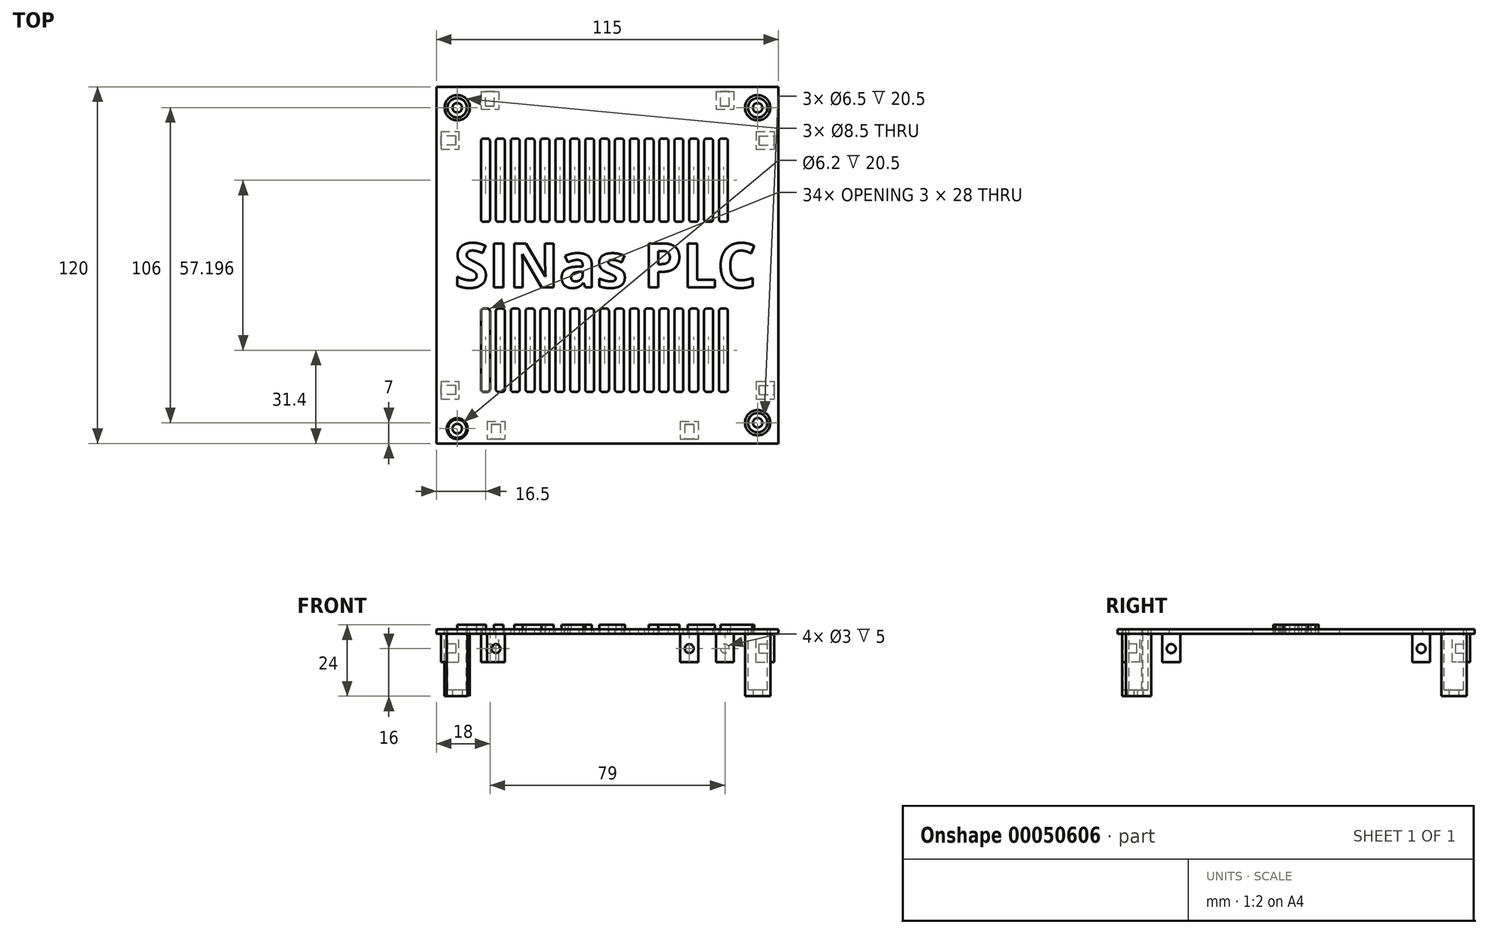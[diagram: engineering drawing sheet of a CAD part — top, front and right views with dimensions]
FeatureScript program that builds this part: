
annotation { "Feature Type Name" : "Feature", "Feature Type Description" : "" }
export const myFeature = defineFeature(function(context is Context, id is Id, definition is map)
    precondition{}
    {
        {
            var Q0;
            Q0=qCreatedBy(makeId("Top.planeOp"),FACE);
            var sketch = newSketch(context, id + "F0", { "sketchPlane" : qUnion([Q0])});
            skLineSegment(sketch, "E0.bottom", {"start": v(-52.5, 65) * mm, "end": v(62.5, 65) * mm});
            skLineSegment(sketch, "E0.top", {"start": v(-52.5, -55) * mm, "end": v(62.5, -55) * mm});
            skLineSegment(sketch, "E0.left", {"start": v(-52.5, 65) * mm, "end": v(-52.5, -55) * mm});
            skLineSegment(sketch, "E0.right", {"start": v(62.5, 65) * mm, "end": v(62.5, -55) * mm});
            skCircle(sketch, "E1", {"center": v(-45.5, 58) * mm, "radius": 4.25 * mm});
            skCircle(sketch, "E2", {"center": v(55.5, 58) * mm, "radius": 4.25 * mm});
            skCircle(sketch, "E3", {"center": v(55.5, -48) * mm, "radius": 4.25 * mm});
            skCircle(sketch, "E4", {"center": v(-45.5, -50) * mm, "radius": 3.5 * mm});
            skText(sketch, "E5", { "text": "SINas PLC", "fontName": "OpenSans-Bold.ttf"});
            skLineSegment(sketch, "E6.bottom", {"start": v(-36.7, 47.6) * mm, "end": v(-35.3, 47.6) * mm});
            skLineSegment(sketch, "E6.top", {"start": v(-36.7, 19.6) * mm, "end": v(-35.3, 19.6) * mm});
            skLineSegment(sketch, "E6.left", {"start": v(-37.5, 46.8) * mm, "end": v(-37.5, 20.4) * mm});
            skLineSegment(sketch, "E6.right", {"start": v(-34.5, 46.8) * mm, "end": v(-34.5, 20.4) * mm});
            skPoint(sketch, "E7.visualSharp", {"position": v(-37.5, 47.6) * mm});
            skArc(sketch, "E7.filletArc", {"start": v(-36.7, 47.6) * mm, "mid": v(-37.27, 47.36) * mm, "end": v(-37.5, 46.8) * mm});
            skPoint(sketch, "E8.visualSharp", {"position": v(-34.5, 47.6) * mm});
            skArc(sketch, "E8.filletArc", {"start": v(-34.5, 46.8) * mm, "mid": v(-34.73, 47.36) * mm, "end": v(-35.3, 47.6) * mm});
            skPoint(sketch, "E9.visualSharp", {"position": v(-37.5, 19.6) * mm});
            skArc(sketch, "E9.filletArc", {"start": v(-37.5, 20.4) * mm, "mid": v(-37.27, 19.83) * mm, "end": v(-36.7, 19.6) * mm});
            skPoint(sketch, "E10.visualSharp", {"position": v(-34.5, 19.6) * mm});
            skArc(sketch, "E10.filletArc", {"start": v(-35.3, 19.6) * mm, "mid": v(-34.73, 19.83) * mm, "end": v(-34.5, 20.4) * mm});
            skLineSegment(sketch, "E11.1.0.0", {"start": v(-29.5, 46.8) * mm, "end": v(-29.5, 20.4) * mm});
            skPoint(sketch, "E11.1.0.1", {"position": v(-32.5, 47.6) * mm});
            skPoint(sketch, "E11.1.0.2", {"position": v(-29.5, 47.6) * mm});
            skPoint(sketch, "E11.1.0.3", {"position": v(-32.5, 19.6) * mm});
            skLineSegment(sketch, "E11.1.0.4", {"start": v(-32.5, 46.8) * mm, "end": v(-32.5, 20.4) * mm});
            skPoint(sketch, "E11.1.0.5", {"position": v(-29.5, 19.6) * mm});
            skArc(sketch, "E11.1.0.6", {"start": v(-29.5, 46.8) * mm, "mid": v(-29.73, 47.36) * mm, "end": v(-30.3, 47.6) * mm});
            skLineSegment(sketch, "E11.1.0.7", {"start": v(-31.7, 19.6) * mm, "end": v(-30.3, 19.6) * mm});
            skLineSegment(sketch, "E11.1.0.8", {"start": v(-31.7, 47.6) * mm, "end": v(-30.3, 47.6) * mm});
            skArc(sketch, "E11.1.0.9", {"start": v(-31.7, 47.6) * mm, "mid": v(-32.27, 47.36) * mm, "end": v(-32.5, 46.8) * mm});
            skArc(sketch, "E11.1.0.10", {"start": v(-32.5, 20.4) * mm, "mid": v(-32.27, 19.83) * mm, "end": v(-31.7, 19.6) * mm});
            skArc(sketch, "E11.1.0.11", {"start": v(-30.3, 19.6) * mm, "mid": v(-29.73, 19.83) * mm, "end": v(-29.5, 20.4) * mm});
            skLineSegment(sketch, "E11.2.0.0", {"start": v(-24.5, 46.8) * mm, "end": v(-24.5, 20.4) * mm});
            skPoint(sketch, "E11.2.0.1", {"position": v(-27.5, 47.6) * mm});
            skPoint(sketch, "E11.2.0.2", {"position": v(-24.5, 47.6) * mm});
            skPoint(sketch, "E11.2.0.3", {"position": v(-27.5, 19.6) * mm});
            skLineSegment(sketch, "E11.2.0.4", {"start": v(-27.5, 46.8) * mm, "end": v(-27.5, 20.4) * mm});
            skPoint(sketch, "E11.2.0.5", {"position": v(-24.5, 19.6) * mm});
            skArc(sketch, "E11.2.0.6", {"start": v(-24.5, 46.8) * mm, "mid": v(-24.73, 47.36) * mm, "end": v(-25.3, 47.6) * mm});
            skLineSegment(sketch, "E11.2.0.7", {"start": v(-26.7, 19.6) * mm, "end": v(-25.3, 19.6) * mm});
            skLineSegment(sketch, "E11.2.0.8", {"start": v(-26.7, 47.6) * mm, "end": v(-25.3, 47.6) * mm});
            skArc(sketch, "E11.2.0.9", {"start": v(-26.7, 47.6) * mm, "mid": v(-27.27, 47.36) * mm, "end": v(-27.5, 46.8) * mm});
            skArc(sketch, "E11.2.0.10", {"start": v(-27.5, 20.4) * mm, "mid": v(-27.27, 19.83) * mm, "end": v(-26.7, 19.6) * mm});
            skArc(sketch, "E11.2.0.11", {"start": v(-25.3, 19.6) * mm, "mid": v(-24.73, 19.83) * mm, "end": v(-24.5, 20.4) * mm});
            skLineSegment(sketch, "E11.3.0.0", {"start": v(-19.5, 46.8) * mm, "end": v(-19.5, 20.4) * mm});
            skPoint(sketch, "E11.3.0.1", {"position": v(-22.5, 47.6) * mm});
            skPoint(sketch, "E11.3.0.2", {"position": v(-19.5, 47.6) * mm});
            skPoint(sketch, "E11.3.0.3", {"position": v(-22.5, 19.6) * mm});
            skLineSegment(sketch, "E11.3.0.4", {"start": v(-22.5, 46.8) * mm, "end": v(-22.5, 20.4) * mm});
            skPoint(sketch, "E11.3.0.5", {"position": v(-19.5, 19.6) * mm});
            skArc(sketch, "E11.3.0.6", {"start": v(-19.5, 46.8) * mm, "mid": v(-19.73, 47.36) * mm, "end": v(-20.3, 47.6) * mm});
            skLineSegment(sketch, "E11.3.0.7", {"start": v(-21.7, 19.6) * mm, "end": v(-20.3, 19.6) * mm});
            skLineSegment(sketch, "E11.3.0.8", {"start": v(-21.7, 47.6) * mm, "end": v(-20.3, 47.6) * mm});
            skArc(sketch, "E11.3.0.9", {"start": v(-21.7, 47.6) * mm, "mid": v(-22.27, 47.36) * mm, "end": v(-22.5, 46.8) * mm});
            skArc(sketch, "E11.3.0.10", {"start": v(-22.5, 20.4) * mm, "mid": v(-22.27, 19.83) * mm, "end": v(-21.7, 19.6) * mm});
            skArc(sketch, "E11.3.0.11", {"start": v(-20.3, 19.6) * mm, "mid": v(-19.73, 19.83) * mm, "end": v(-19.5, 20.4) * mm});
            skLineSegment(sketch, "E11.4.0.0", {"start": v(-14.5, 46.8) * mm, "end": v(-14.5, 20.4) * mm});
            skPoint(sketch, "E11.4.0.1", {"position": v(-17.5, 47.6) * mm});
            skPoint(sketch, "E11.4.0.2", {"position": v(-14.5, 47.6) * mm});
            skPoint(sketch, "E11.4.0.3", {"position": v(-17.5, 19.6) * mm});
            skLineSegment(sketch, "E11.4.0.4", {"start": v(-17.5, 46.8) * mm, "end": v(-17.5, 20.4) * mm});
            skPoint(sketch, "E11.4.0.5", {"position": v(-14.5, 19.6) * mm});
            skArc(sketch, "E11.4.0.6", {"start": v(-14.5, 46.8) * mm, "mid": v(-14.73, 47.36) * mm, "end": v(-15.3, 47.6) * mm});
            skLineSegment(sketch, "E11.4.0.7", {"start": v(-16.7, 19.6) * mm, "end": v(-15.3, 19.6) * mm});
            skLineSegment(sketch, "E11.4.0.8", {"start": v(-16.7, 47.6) * mm, "end": v(-15.3, 47.6) * mm});
            skArc(sketch, "E11.4.0.9", {"start": v(-16.7, 47.6) * mm, "mid": v(-17.27, 47.36) * mm, "end": v(-17.5, 46.8) * mm});
            skArc(sketch, "E11.4.0.10", {"start": v(-17.5, 20.4) * mm, "mid": v(-17.27, 19.83) * mm, "end": v(-16.7, 19.6) * mm});
            skArc(sketch, "E11.4.0.11", {"start": v(-15.3, 19.6) * mm, "mid": v(-14.73, 19.83) * mm, "end": v(-14.5, 20.4) * mm});
            skLineSegment(sketch, "E11.5.0.0", {"start": v(-9.5, 46.8) * mm, "end": v(-9.5, 20.4) * mm});
            skPoint(sketch, "E11.5.0.1", {"position": v(-12.5, 47.6) * mm});
            skPoint(sketch, "E11.5.0.2", {"position": v(-9.5, 47.6) * mm});
            skPoint(sketch, "E11.5.0.3", {"position": v(-12.5, 19.6) * mm});
            skLineSegment(sketch, "E11.5.0.4", {"start": v(-12.5, 46.8) * mm, "end": v(-12.5, 20.4) * mm});
            skPoint(sketch, "E11.5.0.5", {"position": v(-9.5, 19.6) * mm});
            skArc(sketch, "E11.5.0.6", {"start": v(-9.5, 46.8) * mm, "mid": v(-9.73, 47.36) * mm, "end": v(-10.3, 47.6) * mm});
            skLineSegment(sketch, "E11.5.0.7", {"start": v(-11.7, 19.6) * mm, "end": v(-10.3, 19.6) * mm});
            skLineSegment(sketch, "E11.5.0.8", {"start": v(-11.7, 47.6) * mm, "end": v(-10.3, 47.6) * mm});
            skArc(sketch, "E11.5.0.9", {"start": v(-11.7, 47.6) * mm, "mid": v(-12.27, 47.36) * mm, "end": v(-12.5, 46.8) * mm});
            skArc(sketch, "E11.5.0.10", {"start": v(-12.5, 20.4) * mm, "mid": v(-12.27, 19.83) * mm, "end": v(-11.7, 19.6) * mm});
            skArc(sketch, "E11.5.0.11", {"start": v(-10.3, 19.6) * mm, "mid": v(-9.73, 19.83) * mm, "end": v(-9.5, 20.4) * mm});
            skLineSegment(sketch, "E11.6.0.0", {"start": v(-4.5, 46.8) * mm, "end": v(-4.5, 20.4) * mm});
            skPoint(sketch, "E11.6.0.1", {"position": v(-7.5, 47.6) * mm});
            skPoint(sketch, "E11.6.0.2", {"position": v(-4.5, 47.6) * mm});
            skPoint(sketch, "E11.6.0.3", {"position": v(-7.5, 19.6) * mm});
            skLineSegment(sketch, "E11.6.0.4", {"start": v(-7.5, 46.8) * mm, "end": v(-7.5, 20.4) * mm});
            skPoint(sketch, "E11.6.0.5", {"position": v(-4.5, 19.6) * mm});
            skArc(sketch, "E11.6.0.6", {"start": v(-4.5, 46.8) * mm, "mid": v(-4.73, 47.36) * mm, "end": v(-5.3, 47.6) * mm});
            skLineSegment(sketch, "E11.6.0.7", {"start": v(-6.7, 19.6) * mm, "end": v(-5.3, 19.6) * mm});
            skLineSegment(sketch, "E11.6.0.8", {"start": v(-6.7, 47.6) * mm, "end": v(-5.3, 47.6) * mm});
            skArc(sketch, "E11.6.0.9", {"start": v(-6.7, 47.6) * mm, "mid": v(-7.27, 47.36) * mm, "end": v(-7.5, 46.8) * mm});
            skArc(sketch, "E11.6.0.10", {"start": v(-7.5, 20.4) * mm, "mid": v(-7.27, 19.83) * mm, "end": v(-6.7, 19.6) * mm});
            skArc(sketch, "E11.6.0.11", {"start": v(-5.3, 19.6) * mm, "mid": v(-4.73, 19.83) * mm, "end": v(-4.5, 20.4) * mm});
            skLineSegment(sketch, "E11.7.0.0", {"start": v(0.5, 46.8) * mm, "end": v(0.5, 20.4) * mm});
            skPoint(sketch, "E11.7.0.1", {"position": v(-2.5, 47.6) * mm});
            skPoint(sketch, "E11.7.0.2", {"position": v(0.5, 47.6) * mm});
            skPoint(sketch, "E11.7.0.3", {"position": v(-2.5, 19.6) * mm});
            skLineSegment(sketch, "E11.7.0.4", {"start": v(-2.5, 46.8) * mm, "end": v(-2.5, 20.4) * mm});
            skPoint(sketch, "E11.7.0.5", {"position": v(0.5, 19.6) * mm});
            skArc(sketch, "E11.7.0.6", {"start": v(0.5, 46.8) * mm, "mid": v(0.27, 47.36) * mm, "end": v(-0.3, 47.6) * mm});
            skLineSegment(sketch, "E11.7.0.7", {"start": v(-1.7, 19.6) * mm, "end": v(-0.3, 19.6) * mm});
            skLineSegment(sketch, "E11.7.0.8", {"start": v(-1.7, 47.6) * mm, "end": v(-0.3, 47.6) * mm});
            skArc(sketch, "E11.7.0.9", {"start": v(-1.7, 47.6) * mm, "mid": v(-2.27, 47.36) * mm, "end": v(-2.5, 46.8) * mm});
            skArc(sketch, "E11.7.0.10", {"start": v(-2.5, 20.4) * mm, "mid": v(-2.27, 19.83) * mm, "end": v(-1.7, 19.6) * mm});
            skArc(sketch, "E11.7.0.11", {"start": v(-0.3, 19.6) * mm, "mid": v(0.27, 19.83) * mm, "end": v(0.5, 20.4) * mm});
            skLineSegment(sketch, "E11.8.0.0", {"start": v(5.5, 46.8) * mm, "end": v(5.5, 20.4) * mm});
            skPoint(sketch, "E11.8.0.1", {"position": v(2.5, 47.6) * mm});
            skPoint(sketch, "E11.8.0.2", {"position": v(5.5, 47.6) * mm});
            skPoint(sketch, "E11.8.0.3", {"position": v(2.5, 19.6) * mm});
            skLineSegment(sketch, "E11.8.0.4", {"start": v(2.5, 46.8) * mm, "end": v(2.5, 20.4) * mm});
            skPoint(sketch, "E11.8.0.5", {"position": v(5.5, 19.6) * mm});
            skArc(sketch, "E11.8.0.6", {"start": v(5.5, 46.8) * mm, "mid": v(5.27, 47.36) * mm, "end": v(4.7, 47.6) * mm});
            skLineSegment(sketch, "E11.8.0.7", {"start": v(3.3, 19.6) * mm, "end": v(4.7, 19.6) * mm});
            skLineSegment(sketch, "E11.8.0.8", {"start": v(3.3, 47.6) * mm, "end": v(4.7, 47.6) * mm});
            skArc(sketch, "E11.8.0.9", {"start": v(3.3, 47.6) * mm, "mid": v(2.73, 47.36) * mm, "end": v(2.5, 46.8) * mm});
            skArc(sketch, "E11.8.0.10", {"start": v(2.5, 20.4) * mm, "mid": v(2.73, 19.83) * mm, "end": v(3.3, 19.6) * mm});
            skArc(sketch, "E11.8.0.11", {"start": v(4.7, 19.6) * mm, "mid": v(5.27, 19.83) * mm, "end": v(5.5, 20.4) * mm});
            skLineSegment(sketch, "E11.9.0.0", {"start": v(10.5, 46.8) * mm, "end": v(10.5, 20.4) * mm});
            skPoint(sketch, "E11.9.0.1", {"position": v(7.5, 47.6) * mm});
            skPoint(sketch, "E11.9.0.2", {"position": v(10.5, 47.6) * mm});
            skPoint(sketch, "E11.9.0.3", {"position": v(7.5, 19.6) * mm});
            skLineSegment(sketch, "E11.9.0.4", {"start": v(7.5, 46.8) * mm, "end": v(7.5, 20.4) * mm});
            skPoint(sketch, "E11.9.0.5", {"position": v(10.5, 19.6) * mm});
            skArc(sketch, "E11.9.0.6", {"start": v(10.5, 46.8) * mm, "mid": v(10.27, 47.36) * mm, "end": v(9.7, 47.6) * mm});
            skLineSegment(sketch, "E11.9.0.7", {"start": v(8.3, 19.6) * mm, "end": v(9.7, 19.6) * mm});
            skLineSegment(sketch, "E11.9.0.8", {"start": v(8.3, 47.6) * mm, "end": v(9.7, 47.6) * mm});
            skArc(sketch, "E11.9.0.9", {"start": v(8.3, 47.6) * mm, "mid": v(7.73, 47.36) * mm, "end": v(7.5, 46.8) * mm});
            skArc(sketch, "E11.9.0.10", {"start": v(7.5, 20.4) * mm, "mid": v(7.73, 19.83) * mm, "end": v(8.3, 19.6) * mm});
            skArc(sketch, "E11.9.0.11", {"start": v(9.7, 19.6) * mm, "mid": v(10.27, 19.83) * mm, "end": v(10.5, 20.4) * mm});
            skLineSegment(sketch, "E11.10.0.0", {"start": v(15.5, 46.8) * mm, "end": v(15.5, 20.4) * mm});
            skPoint(sketch, "E11.10.0.1", {"position": v(12.5, 47.6) * mm});
            skPoint(sketch, "E11.10.0.2", {"position": v(15.5, 47.6) * mm});
            skPoint(sketch, "E11.10.0.3", {"position": v(12.5, 19.6) * mm});
            skLineSegment(sketch, "E11.10.0.4", {"start": v(12.5, 46.8) * mm, "end": v(12.5, 20.4) * mm});
            skPoint(sketch, "E11.10.0.5", {"position": v(15.5, 19.6) * mm});
            skArc(sketch, "E11.10.0.6", {"start": v(15.5, 46.8) * mm, "mid": v(15.27, 47.36) * mm, "end": v(14.7, 47.6) * mm});
            skLineSegment(sketch, "E11.10.0.7", {"start": v(13.3, 19.6) * mm, "end": v(14.7, 19.6) * mm});
            skLineSegment(sketch, "E11.10.0.8", {"start": v(13.3, 47.6) * mm, "end": v(14.7, 47.6) * mm});
            skArc(sketch, "E11.10.0.9", {"start": v(13.3, 47.6) * mm, "mid": v(12.73, 47.36) * mm, "end": v(12.5, 46.8) * mm});
            skArc(sketch, "E11.10.0.10", {"start": v(12.5, 20.4) * mm, "mid": v(12.73, 19.83) * mm, "end": v(13.3, 19.6) * mm});
            skArc(sketch, "E11.10.0.11", {"start": v(14.7, 19.6) * mm, "mid": v(15.27, 19.83) * mm, "end": v(15.5, 20.4) * mm});
            skLineSegment(sketch, "E11.11.0.0", {"start": v(20.5, 46.8) * mm, "end": v(20.5, 20.4) * mm});
            skPoint(sketch, "E11.11.0.1", {"position": v(17.5, 47.6) * mm});
            skPoint(sketch, "E11.11.0.2", {"position": v(20.5, 47.6) * mm});
            skPoint(sketch, "E11.11.0.3", {"position": v(17.5, 19.6) * mm});
            skLineSegment(sketch, "E11.11.0.4", {"start": v(17.5, 46.8) * mm, "end": v(17.5, 20.4) * mm});
            skPoint(sketch, "E11.11.0.5", {"position": v(20.5, 19.6) * mm});
            skArc(sketch, "E11.11.0.6", {"start": v(20.5, 46.8) * mm, "mid": v(20.27, 47.36) * mm, "end": v(19.7, 47.6) * mm});
            skLineSegment(sketch, "E11.11.0.7", {"start": v(18.3, 19.6) * mm, "end": v(19.7, 19.6) * mm});
            skLineSegment(sketch, "E11.11.0.8", {"start": v(18.3, 47.6) * mm, "end": v(19.7, 47.6) * mm});
            skArc(sketch, "E11.11.0.9", {"start": v(18.3, 47.6) * mm, "mid": v(17.73, 47.36) * mm, "end": v(17.5, 46.8) * mm});
            skArc(sketch, "E11.11.0.10", {"start": v(17.5, 20.4) * mm, "mid": v(17.73, 19.83) * mm, "end": v(18.3, 19.6) * mm});
            skArc(sketch, "E11.11.0.11", {"start": v(19.7, 19.6) * mm, "mid": v(20.27, 19.83) * mm, "end": v(20.5, 20.4) * mm});
            skLineSegment(sketch, "E11.12.0.0", {"start": v(25.5, 46.8) * mm, "end": v(25.5, 20.4) * mm});
            skPoint(sketch, "E11.12.0.1", {"position": v(22.5, 47.6) * mm});
            skPoint(sketch, "E11.12.0.2", {"position": v(25.5, 47.6) * mm});
            skPoint(sketch, "E11.12.0.3", {"position": v(22.5, 19.6) * mm});
            skLineSegment(sketch, "E11.12.0.4", {"start": v(22.5, 46.8) * mm, "end": v(22.5, 20.4) * mm});
            skPoint(sketch, "E11.12.0.5", {"position": v(25.5, 19.6) * mm});
            skArc(sketch, "E11.12.0.6", {"start": v(25.5, 46.8) * mm, "mid": v(25.27, 47.36) * mm, "end": v(24.7, 47.6) * mm});
            skLineSegment(sketch, "E11.12.0.7", {"start": v(23.3, 19.6) * mm, "end": v(24.7, 19.6) * mm});
            skLineSegment(sketch, "E11.12.0.8", {"start": v(23.3, 47.6) * mm, "end": v(24.7, 47.6) * mm});
            skArc(sketch, "E11.12.0.9", {"start": v(23.3, 47.6) * mm, "mid": v(22.73, 47.36) * mm, "end": v(22.5, 46.8) * mm});
            skArc(sketch, "E11.12.0.10", {"start": v(22.5, 20.4) * mm, "mid": v(22.73, 19.83) * mm, "end": v(23.3, 19.6) * mm});
            skArc(sketch, "E11.12.0.11", {"start": v(24.7, 19.6) * mm, "mid": v(25.27, 19.83) * mm, "end": v(25.5, 20.4) * mm});
            skLineSegment(sketch, "E11.13.0.0", {"start": v(30.5, 46.8) * mm, "end": v(30.5, 20.4) * mm});
            skPoint(sketch, "E11.13.0.1", {"position": v(27.5, 47.6) * mm});
            skPoint(sketch, "E11.13.0.2", {"position": v(30.5, 47.6) * mm});
            skPoint(sketch, "E11.13.0.3", {"position": v(27.5, 19.6) * mm});
            skLineSegment(sketch, "E11.13.0.4", {"start": v(27.5, 46.8) * mm, "end": v(27.5, 20.4) * mm});
            skPoint(sketch, "E11.13.0.5", {"position": v(30.5, 19.6) * mm});
            skArc(sketch, "E11.13.0.6", {"start": v(30.5, 46.8) * mm, "mid": v(30.27, 47.36) * mm, "end": v(29.7, 47.6) * mm});
            skLineSegment(sketch, "E11.13.0.7", {"start": v(28.3, 19.6) * mm, "end": v(29.7, 19.6) * mm});
            skLineSegment(sketch, "E11.13.0.8", {"start": v(28.3, 47.6) * mm, "end": v(29.7, 47.6) * mm});
            skArc(sketch, "E11.13.0.9", {"start": v(28.3, 47.6) * mm, "mid": v(27.73, 47.36) * mm, "end": v(27.5, 46.8) * mm});
            skArc(sketch, "E11.13.0.10", {"start": v(27.5, 20.4) * mm, "mid": v(27.73, 19.83) * mm, "end": v(28.3, 19.6) * mm});
            skArc(sketch, "E11.13.0.11", {"start": v(29.7, 19.6) * mm, "mid": v(30.27, 19.83) * mm, "end": v(30.5, 20.4) * mm});
            skLineSegment(sketch, "E11.14.0.0", {"start": v(35.5, 46.8) * mm, "end": v(35.5, 20.4) * mm});
            skPoint(sketch, "E11.14.0.1", {"position": v(32.5, 47.6) * mm});
            skPoint(sketch, "E11.14.0.2", {"position": v(35.5, 47.6) * mm});
            skPoint(sketch, "E11.14.0.3", {"position": v(32.5, 19.6) * mm});
            skLineSegment(sketch, "E11.14.0.4", {"start": v(32.5, 46.8) * mm, "end": v(32.5, 20.4) * mm});
            skPoint(sketch, "E11.14.0.5", {"position": v(35.5, 19.6) * mm});
            skArc(sketch, "E11.14.0.6", {"start": v(35.5, 46.8) * mm, "mid": v(35.27, 47.36) * mm, "end": v(34.7, 47.6) * mm});
            skLineSegment(sketch, "E11.14.0.7", {"start": v(33.3, 19.6) * mm, "end": v(34.7, 19.6) * mm});
            skLineSegment(sketch, "E11.14.0.8", {"start": v(33.3, 47.6) * mm, "end": v(34.7, 47.6) * mm});
            skArc(sketch, "E11.14.0.9", {"start": v(33.3, 47.6) * mm, "mid": v(32.73, 47.36) * mm, "end": v(32.5, 46.8) * mm});
            skArc(sketch, "E11.14.0.10", {"start": v(32.5, 20.4) * mm, "mid": v(32.73, 19.83) * mm, "end": v(33.3, 19.6) * mm});
            skArc(sketch, "E11.14.0.11", {"start": v(34.7, 19.6) * mm, "mid": v(35.27, 19.83) * mm, "end": v(35.5, 20.4) * mm});
            skLineSegment(sketch, "E11.15.0.0", {"start": v(40.5, 46.8) * mm, "end": v(40.5, 20.4) * mm});
            skPoint(sketch, "E11.15.0.1", {"position": v(37.5, 47.6) * mm});
            skPoint(sketch, "E11.15.0.2", {"position": v(40.5, 47.6) * mm});
            skPoint(sketch, "E11.15.0.3", {"position": v(37.5, 19.6) * mm});
            skLineSegment(sketch, "E11.15.0.4", {"start": v(37.5, 46.8) * mm, "end": v(37.5, 20.4) * mm});
            skPoint(sketch, "E11.15.0.5", {"position": v(40.5, 19.6) * mm});
            skArc(sketch, "E11.15.0.6", {"start": v(40.5, 46.8) * mm, "mid": v(40.27, 47.36) * mm, "end": v(39.7, 47.6) * mm});
            skLineSegment(sketch, "E11.15.0.7", {"start": v(38.3, 19.6) * mm, "end": v(39.7, 19.6) * mm});
            skLineSegment(sketch, "E11.15.0.8", {"start": v(38.3, 47.6) * mm, "end": v(39.7, 47.6) * mm});
            skArc(sketch, "E11.15.0.9", {"start": v(38.3, 47.6) * mm, "mid": v(37.73, 47.36) * mm, "end": v(37.5, 46.8) * mm});
            skArc(sketch, "E11.15.0.10", {"start": v(37.5, 20.4) * mm, "mid": v(37.73, 19.83) * mm, "end": v(38.3, 19.6) * mm});
            skArc(sketch, "E11.15.0.11", {"start": v(39.7, 19.6) * mm, "mid": v(40.27, 19.83) * mm, "end": v(40.5, 20.4) * mm});
            skLineSegment(sketch, "E11.16.0.0", {"start": v(45.5, 46.8) * mm, "end": v(45.5, 20.4) * mm});
            skPoint(sketch, "E11.16.0.1", {"position": v(42.5, 47.6) * mm});
            skPoint(sketch, "E11.16.0.2", {"position": v(45.5, 47.6) * mm});
            skPoint(sketch, "E11.16.0.3", {"position": v(42.5, 19.6) * mm});
            skLineSegment(sketch, "E11.16.0.4", {"start": v(42.5, 46.8) * mm, "end": v(42.5, 20.4) * mm});
            skPoint(sketch, "E11.16.0.5", {"position": v(45.5, 19.6) * mm});
            skArc(sketch, "E11.16.0.6", {"start": v(45.5, 46.8) * mm, "mid": v(45.27, 47.36) * mm, "end": v(44.7, 47.6) * mm});
            skLineSegment(sketch, "E11.16.0.7", {"start": v(43.3, 19.6) * mm, "end": v(44.7, 19.6) * mm});
            skLineSegment(sketch, "E11.16.0.8", {"start": v(43.3, 47.6) * mm, "end": v(44.7, 47.6) * mm});
            skArc(sketch, "E11.16.0.9", {"start": v(43.3, 47.6) * mm, "mid": v(42.73, 47.36) * mm, "end": v(42.5, 46.8) * mm});
            skArc(sketch, "E11.16.0.10", {"start": v(42.5, 20.4) * mm, "mid": v(42.73, 19.83) * mm, "end": v(43.3, 19.6) * mm});
            skArc(sketch, "E11.16.0.11", {"start": v(44.7, 19.6) * mm, "mid": v(45.27, 19.83) * mm, "end": v(45.5, 20.4) * mm});
            skLineSegment(sketch, "E11.direction1", {"start": v(-34.5, 20.4) * mm, "end": v(-29.5, 20.4) * mm, "construction": true});
            skLineSegment(sketch, "E12.bottom", {"start": v(-36.7, -9.6) * mm, "end": v(-35.3, -9.6) * mm});
            skLineSegment(sketch, "E12.top", {"start": v(-36.7, -37.6) * mm, "end": v(-35.3, -37.6) * mm});
            skLineSegment(sketch, "E12.left", {"start": v(-37.5, -10.4) * mm, "end": v(-37.5, -36.8) * mm});
            skLineSegment(sketch, "E12.right", {"start": v(-34.5, -10.4) * mm, "end": v(-34.5, -36.8) * mm});
            skPoint(sketch, "E13.visualSharp", {"position": v(-37.5, -9.6) * mm});
            skArc(sketch, "E13.filletArc", {"start": v(-36.7, -9.6) * mm, "mid": v(-37.27, -9.83) * mm, "end": v(-37.5, -10.4) * mm});
            skPoint(sketch, "E14.visualSharp", {"position": v(-34.5, -9.6) * mm});
            skArc(sketch, "E14.filletArc", {"start": v(-34.5, -10.4) * mm, "mid": v(-34.73, -9.83) * mm, "end": v(-35.3, -9.6) * mm});
            skPoint(sketch, "E15.visualSharp", {"position": v(-37.5, -37.6) * mm});
            skArc(sketch, "E15.filletArc", {"start": v(-37.5, -36.8) * mm, "mid": v(-37.27, -37.37) * mm, "end": v(-36.7, -37.6) * mm});
            skPoint(sketch, "E16.visualSharp", {"position": v(-34.5, -37.6) * mm});
            skArc(sketch, "E16.filletArc", {"start": v(-35.3, -37.6) * mm, "mid": v(-34.73, -37.37) * mm, "end": v(-34.5, -36.8) * mm});
            skPoint(sketch, "E17.1.0.0", {"position": v(-29.5, -37.6) * mm});
            skPoint(sketch, "E17.1.0.1", {"position": v(-32.5, -37.6) * mm});
            skPoint(sketch, "E17.1.0.2", {"position": v(-29.5, -9.6) * mm});
            skPoint(sketch, "E17.1.0.3", {"position": v(-32.5, -9.6) * mm});
            skLineSegment(sketch, "E17.1.0.4", {"start": v(-32.5, -10.4) * mm, "end": v(-32.5, -36.8) * mm});
            skLineSegment(sketch, "E17.1.0.5", {"start": v(-29.5, -10.4) * mm, "end": v(-29.5, -36.8) * mm});
            skArc(sketch, "E17.1.0.6", {"start": v(-30.3, -37.6) * mm, "mid": v(-29.73, -37.37) * mm, "end": v(-29.5, -36.8) * mm});
            skArc(sketch, "E17.1.0.7", {"start": v(-32.5, -36.8) * mm, "mid": v(-32.27, -37.37) * mm, "end": v(-31.7, -37.6) * mm});
            skArc(sketch, "E17.1.0.8", {"start": v(-29.5, -10.4) * mm, "mid": v(-29.73, -9.83) * mm, "end": v(-30.3, -9.6) * mm});
            skArc(sketch, "E17.1.0.9", {"start": v(-31.7, -9.6) * mm, "mid": v(-32.27, -9.83) * mm, "end": v(-32.5, -10.4) * mm});
            skLineSegment(sketch, "E17.1.0.10", {"start": v(-31.7, -9.6) * mm, "end": v(-30.3, -9.6) * mm});
            skLineSegment(sketch, "E17.1.0.11", {"start": v(-31.7, -37.6) * mm, "end": v(-30.3, -37.6) * mm});
            skPoint(sketch, "E17.2.0.0", {"position": v(-24.5, -37.6) * mm});
            skPoint(sketch, "E17.2.0.1", {"position": v(-27.5, -37.6) * mm});
            skPoint(sketch, "E17.2.0.2", {"position": v(-24.5, -9.6) * mm});
            skPoint(sketch, "E17.2.0.3", {"position": v(-27.5, -9.6) * mm});
            skLineSegment(sketch, "E17.2.0.4", {"start": v(-27.5, -10.4) * mm, "end": v(-27.5, -36.8) * mm});
            skLineSegment(sketch, "E17.2.0.5", {"start": v(-24.5, -10.4) * mm, "end": v(-24.5, -36.8) * mm});
            skArc(sketch, "E17.2.0.6", {"start": v(-25.3, -37.6) * mm, "mid": v(-24.73, -37.37) * mm, "end": v(-24.5, -36.8) * mm});
            skArc(sketch, "E17.2.0.7", {"start": v(-27.5, -36.8) * mm, "mid": v(-27.27, -37.37) * mm, "end": v(-26.7, -37.6) * mm});
            skArc(sketch, "E17.2.0.8", {"start": v(-24.5, -10.4) * mm, "mid": v(-24.73, -9.83) * mm, "end": v(-25.3, -9.6) * mm});
            skArc(sketch, "E17.2.0.9", {"start": v(-26.7, -9.6) * mm, "mid": v(-27.27, -9.83) * mm, "end": v(-27.5, -10.4) * mm});
            skLineSegment(sketch, "E17.2.0.10", {"start": v(-26.7, -9.6) * mm, "end": v(-25.3, -9.6) * mm});
            skLineSegment(sketch, "E17.2.0.11", {"start": v(-26.7, -37.6) * mm, "end": v(-25.3, -37.6) * mm});
            skPoint(sketch, "E17.3.0.0", {"position": v(-19.5, -37.6) * mm});
            skPoint(sketch, "E17.3.0.1", {"position": v(-22.5, -37.6) * mm});
            skPoint(sketch, "E17.3.0.2", {"position": v(-19.5, -9.6) * mm});
            skPoint(sketch, "E17.3.0.3", {"position": v(-22.5, -9.6) * mm});
            skLineSegment(sketch, "E17.3.0.4", {"start": v(-22.5, -10.4) * mm, "end": v(-22.5, -36.8) * mm});
            skLineSegment(sketch, "E17.3.0.5", {"start": v(-19.5, -10.4) * mm, "end": v(-19.5, -36.8) * mm});
            skArc(sketch, "E17.3.0.6", {"start": v(-20.3, -37.6) * mm, "mid": v(-19.73, -37.37) * mm, "end": v(-19.5, -36.8) * mm});
            skArc(sketch, "E17.3.0.7", {"start": v(-22.5, -36.8) * mm, "mid": v(-22.27, -37.37) * mm, "end": v(-21.7, -37.6) * mm});
            skArc(sketch, "E17.3.0.8", {"start": v(-19.5, -10.4) * mm, "mid": v(-19.73, -9.83) * mm, "end": v(-20.3, -9.6) * mm});
            skArc(sketch, "E17.3.0.9", {"start": v(-21.7, -9.6) * mm, "mid": v(-22.27, -9.83) * mm, "end": v(-22.5, -10.4) * mm});
            skLineSegment(sketch, "E17.3.0.10", {"start": v(-21.7, -9.6) * mm, "end": v(-20.3, -9.6) * mm});
            skLineSegment(sketch, "E17.3.0.11", {"start": v(-21.7, -37.6) * mm, "end": v(-20.3, -37.6) * mm});
            skPoint(sketch, "E17.4.0.0", {"position": v(-14.5, -37.6) * mm});
            skPoint(sketch, "E17.4.0.1", {"position": v(-17.5, -37.6) * mm});
            skPoint(sketch, "E17.4.0.2", {"position": v(-14.5, -9.6) * mm});
            skPoint(sketch, "E17.4.0.3", {"position": v(-17.5, -9.6) * mm});
            skLineSegment(sketch, "E17.4.0.4", {"start": v(-17.5, -10.4) * mm, "end": v(-17.5, -36.8) * mm});
            skLineSegment(sketch, "E17.4.0.5", {"start": v(-14.5, -10.4) * mm, "end": v(-14.5, -36.8) * mm});
            skArc(sketch, "E17.4.0.6", {"start": v(-15.3, -37.6) * mm, "mid": v(-14.73, -37.37) * mm, "end": v(-14.5, -36.8) * mm});
            skArc(sketch, "E17.4.0.7", {"start": v(-17.5, -36.8) * mm, "mid": v(-17.27, -37.37) * mm, "end": v(-16.7, -37.6) * mm});
            skArc(sketch, "E17.4.0.8", {"start": v(-14.5, -10.4) * mm, "mid": v(-14.73, -9.83) * mm, "end": v(-15.3, -9.6) * mm});
            skArc(sketch, "E17.4.0.9", {"start": v(-16.7, -9.6) * mm, "mid": v(-17.27, -9.83) * mm, "end": v(-17.5, -10.4) * mm});
            skLineSegment(sketch, "E17.4.0.10", {"start": v(-16.7, -9.6) * mm, "end": v(-15.3, -9.6) * mm});
            skLineSegment(sketch, "E17.4.0.11", {"start": v(-16.7, -37.6) * mm, "end": v(-15.3, -37.6) * mm});
            skPoint(sketch, "E17.5.0.0", {"position": v(-9.5, -37.6) * mm});
            skPoint(sketch, "E17.5.0.1", {"position": v(-12.5, -37.6) * mm});
            skPoint(sketch, "E17.5.0.2", {"position": v(-9.5, -9.6) * mm});
            skPoint(sketch, "E17.5.0.3", {"position": v(-12.5, -9.6) * mm});
            skLineSegment(sketch, "E17.5.0.4", {"start": v(-12.5, -10.4) * mm, "end": v(-12.5, -36.8) * mm});
            skLineSegment(sketch, "E17.5.0.5", {"start": v(-9.5, -10.4) * mm, "end": v(-9.5, -36.8) * mm});
            skArc(sketch, "E17.5.0.6", {"start": v(-10.3, -37.6) * mm, "mid": v(-9.73, -37.37) * mm, "end": v(-9.5, -36.8) * mm});
            skArc(sketch, "E17.5.0.7", {"start": v(-12.5, -36.8) * mm, "mid": v(-12.27, -37.37) * mm, "end": v(-11.7, -37.6) * mm});
            skArc(sketch, "E17.5.0.8", {"start": v(-9.5, -10.4) * mm, "mid": v(-9.73, -9.83) * mm, "end": v(-10.3, -9.6) * mm});
            skArc(sketch, "E17.5.0.9", {"start": v(-11.7, -9.6) * mm, "mid": v(-12.27, -9.83) * mm, "end": v(-12.5, -10.4) * mm});
            skLineSegment(sketch, "E17.5.0.10", {"start": v(-11.7, -9.6) * mm, "end": v(-10.3, -9.6) * mm});
            skLineSegment(sketch, "E17.5.0.11", {"start": v(-11.7, -37.6) * mm, "end": v(-10.3, -37.6) * mm});
            skPoint(sketch, "E17.6.0.0", {"position": v(-4.5, -37.6) * mm});
            skPoint(sketch, "E17.6.0.1", {"position": v(-7.5, -37.6) * mm});
            skPoint(sketch, "E17.6.0.2", {"position": v(-4.5, -9.6) * mm});
            skPoint(sketch, "E17.6.0.3", {"position": v(-7.5, -9.6) * mm});
            skLineSegment(sketch, "E17.6.0.4", {"start": v(-7.5, -10.4) * mm, "end": v(-7.5, -36.8) * mm});
            skLineSegment(sketch, "E17.6.0.5", {"start": v(-4.5, -10.4) * mm, "end": v(-4.5, -36.8) * mm});
            skArc(sketch, "E17.6.0.6", {"start": v(-5.3, -37.6) * mm, "mid": v(-4.73, -37.37) * mm, "end": v(-4.5, -36.8) * mm});
            skArc(sketch, "E17.6.0.7", {"start": v(-7.5, -36.8) * mm, "mid": v(-7.27, -37.37) * mm, "end": v(-6.7, -37.6) * mm});
            skArc(sketch, "E17.6.0.8", {"start": v(-4.5, -10.4) * mm, "mid": v(-4.73, -9.83) * mm, "end": v(-5.3, -9.6) * mm});
            skArc(sketch, "E17.6.0.9", {"start": v(-6.7, -9.6) * mm, "mid": v(-7.27, -9.83) * mm, "end": v(-7.5, -10.4) * mm});
            skLineSegment(sketch, "E17.6.0.10", {"start": v(-6.7, -9.6) * mm, "end": v(-5.3, -9.6) * mm});
            skLineSegment(sketch, "E17.6.0.11", {"start": v(-6.7, -37.6) * mm, "end": v(-5.3, -37.6) * mm});
            skPoint(sketch, "E17.7.0.0", {"position": v(0.5, -37.6) * mm});
            skPoint(sketch, "E17.7.0.1", {"position": v(-2.5, -37.6) * mm});
            skPoint(sketch, "E17.7.0.2", {"position": v(0.5, -9.6) * mm});
            skPoint(sketch, "E17.7.0.3", {"position": v(-2.5, -9.6) * mm});
            skLineSegment(sketch, "E17.7.0.4", {"start": v(-2.5, -10.4) * mm, "end": v(-2.5, -36.8) * mm});
            skLineSegment(sketch, "E17.7.0.5", {"start": v(0.5, -10.4) * mm, "end": v(0.5, -36.8) * mm});
            skArc(sketch, "E17.7.0.6", {"start": v(-0.3, -37.6) * mm, "mid": v(0.27, -37.37) * mm, "end": v(0.5, -36.8) * mm});
            skArc(sketch, "E17.7.0.7", {"start": v(-2.5, -36.8) * mm, "mid": v(-2.27, -37.37) * mm, "end": v(-1.7, -37.6) * mm});
            skArc(sketch, "E17.7.0.8", {"start": v(0.5, -10.4) * mm, "mid": v(0.27, -9.83) * mm, "end": v(-0.3, -9.6) * mm});
            skArc(sketch, "E17.7.0.9", {"start": v(-1.7, -9.6) * mm, "mid": v(-2.27, -9.83) * mm, "end": v(-2.5, -10.4) * mm});
            skLineSegment(sketch, "E17.7.0.10", {"start": v(-1.7, -9.6) * mm, "end": v(-0.3, -9.6) * mm});
            skLineSegment(sketch, "E17.7.0.11", {"start": v(-1.7, -37.6) * mm, "end": v(-0.3, -37.6) * mm});
            skPoint(sketch, "E17.8.0.0", {"position": v(5.5, -37.6) * mm});
            skPoint(sketch, "E17.8.0.1", {"position": v(2.5, -37.6) * mm});
            skPoint(sketch, "E17.8.0.2", {"position": v(5.5, -9.6) * mm});
            skPoint(sketch, "E17.8.0.3", {"position": v(2.5, -9.6) * mm});
            skLineSegment(sketch, "E17.8.0.4", {"start": v(2.5, -10.4) * mm, "end": v(2.5, -36.8) * mm});
            skLineSegment(sketch, "E17.8.0.5", {"start": v(5.5, -10.4) * mm, "end": v(5.5, -36.8) * mm});
            skArc(sketch, "E17.8.0.6", {"start": v(4.7, -37.6) * mm, "mid": v(5.27, -37.37) * mm, "end": v(5.5, -36.8) * mm});
            skArc(sketch, "E17.8.0.7", {"start": v(2.5, -36.8) * mm, "mid": v(2.73, -37.37) * mm, "end": v(3.3, -37.6) * mm});
            skArc(sketch, "E17.8.0.8", {"start": v(5.5, -10.4) * mm, "mid": v(5.27, -9.83) * mm, "end": v(4.7, -9.6) * mm});
            skArc(sketch, "E17.8.0.9", {"start": v(3.3, -9.6) * mm, "mid": v(2.73, -9.83) * mm, "end": v(2.5, -10.4) * mm});
            skLineSegment(sketch, "E17.8.0.10", {"start": v(3.3, -9.6) * mm, "end": v(4.7, -9.6) * mm});
            skLineSegment(sketch, "E17.8.0.11", {"start": v(3.3, -37.6) * mm, "end": v(4.7, -37.6) * mm});
            skPoint(sketch, "E17.9.0.0", {"position": v(10.5, -37.6) * mm});
            skPoint(sketch, "E17.9.0.1", {"position": v(7.5, -37.6) * mm});
            skPoint(sketch, "E17.9.0.2", {"position": v(10.5, -9.6) * mm});
            skPoint(sketch, "E17.9.0.3", {"position": v(7.5, -9.6) * mm});
            skLineSegment(sketch, "E17.9.0.4", {"start": v(7.5, -10.4) * mm, "end": v(7.5, -36.8) * mm});
            skLineSegment(sketch, "E17.9.0.5", {"start": v(10.5, -10.4) * mm, "end": v(10.5, -36.8) * mm});
            skArc(sketch, "E17.9.0.6", {"start": v(9.7, -37.6) * mm, "mid": v(10.27, -37.37) * mm, "end": v(10.5, -36.8) * mm});
            skArc(sketch, "E17.9.0.7", {"start": v(7.5, -36.8) * mm, "mid": v(7.73, -37.37) * mm, "end": v(8.3, -37.6) * mm});
            skArc(sketch, "E17.9.0.8", {"start": v(10.5, -10.4) * mm, "mid": v(10.27, -9.83) * mm, "end": v(9.7, -9.6) * mm});
            skArc(sketch, "E17.9.0.9", {"start": v(8.3, -9.6) * mm, "mid": v(7.73, -9.83) * mm, "end": v(7.5, -10.4) * mm});
            skLineSegment(sketch, "E17.9.0.10", {"start": v(8.3, -9.6) * mm, "end": v(9.7, -9.6) * mm});
            skLineSegment(sketch, "E17.9.0.11", {"start": v(8.3, -37.6) * mm, "end": v(9.7, -37.6) * mm});
            skPoint(sketch, "E17.10.0.0", {"position": v(15.5, -37.6) * mm});
            skPoint(sketch, "E17.10.0.1", {"position": v(12.5, -37.6) * mm});
            skPoint(sketch, "E17.10.0.2", {"position": v(15.5, -9.6) * mm});
            skPoint(sketch, "E17.10.0.3", {"position": v(12.5, -9.6) * mm});
            skLineSegment(sketch, "E17.10.0.4", {"start": v(12.5, -10.4) * mm, "end": v(12.5, -36.8) * mm});
            skLineSegment(sketch, "E17.10.0.5", {"start": v(15.5, -10.4) * mm, "end": v(15.5, -36.8) * mm});
            skArc(sketch, "E17.10.0.6", {"start": v(14.7, -37.6) * mm, "mid": v(15.27, -37.37) * mm, "end": v(15.5, -36.8) * mm});
            skArc(sketch, "E17.10.0.7", {"start": v(12.5, -36.8) * mm, "mid": v(12.73, -37.37) * mm, "end": v(13.3, -37.6) * mm});
            skArc(sketch, "E17.10.0.8", {"start": v(15.5, -10.4) * mm, "mid": v(15.27, -9.83) * mm, "end": v(14.7, -9.6) * mm});
            skArc(sketch, "E17.10.0.9", {"start": v(13.3, -9.6) * mm, "mid": v(12.73, -9.83) * mm, "end": v(12.5, -10.4) * mm});
            skLineSegment(sketch, "E17.10.0.10", {"start": v(13.3, -9.6) * mm, "end": v(14.7, -9.6) * mm});
            skLineSegment(sketch, "E17.10.0.11", {"start": v(13.3, -37.6) * mm, "end": v(14.7, -37.6) * mm});
            skPoint(sketch, "E17.11.0.0", {"position": v(20.5, -37.6) * mm});
            skPoint(sketch, "E17.11.0.1", {"position": v(17.5, -37.6) * mm});
            skPoint(sketch, "E17.11.0.2", {"position": v(20.5, -9.6) * mm});
            skPoint(sketch, "E17.11.0.3", {"position": v(17.5, -9.6) * mm});
            skLineSegment(sketch, "E17.11.0.4", {"start": v(17.5, -10.4) * mm, "end": v(17.5, -36.8) * mm});
            skLineSegment(sketch, "E17.11.0.5", {"start": v(20.5, -10.4) * mm, "end": v(20.5, -36.8) * mm});
            skArc(sketch, "E17.11.0.6", {"start": v(19.7, -37.6) * mm, "mid": v(20.27, -37.37) * mm, "end": v(20.5, -36.8) * mm});
            skArc(sketch, "E17.11.0.7", {"start": v(17.5, -36.8) * mm, "mid": v(17.73, -37.37) * mm, "end": v(18.3, -37.6) * mm});
            skArc(sketch, "E17.11.0.8", {"start": v(20.5, -10.4) * mm, "mid": v(20.27, -9.83) * mm, "end": v(19.7, -9.6) * mm});
            skArc(sketch, "E17.11.0.9", {"start": v(18.3, -9.6) * mm, "mid": v(17.73, -9.83) * mm, "end": v(17.5, -10.4) * mm});
            skLineSegment(sketch, "E17.11.0.10", {"start": v(18.3, -9.6) * mm, "end": v(19.7, -9.6) * mm});
            skLineSegment(sketch, "E17.11.0.11", {"start": v(18.3, -37.6) * mm, "end": v(19.7, -37.6) * mm});
            skPoint(sketch, "E17.12.0.0", {"position": v(25.5, -37.6) * mm});
            skPoint(sketch, "E17.12.0.1", {"position": v(22.5, -37.6) * mm});
            skPoint(sketch, "E17.12.0.2", {"position": v(25.5, -9.6) * mm});
            skPoint(sketch, "E17.12.0.3", {"position": v(22.5, -9.6) * mm});
            skLineSegment(sketch, "E17.12.0.4", {"start": v(22.5, -10.4) * mm, "end": v(22.5, -36.8) * mm});
            skLineSegment(sketch, "E17.12.0.5", {"start": v(25.5, -10.4) * mm, "end": v(25.5, -36.8) * mm});
            skArc(sketch, "E17.12.0.6", {"start": v(24.7, -37.6) * mm, "mid": v(25.27, -37.37) * mm, "end": v(25.5, -36.8) * mm});
            skArc(sketch, "E17.12.0.7", {"start": v(22.5, -36.8) * mm, "mid": v(22.73, -37.37) * mm, "end": v(23.3, -37.6) * mm});
            skArc(sketch, "E17.12.0.8", {"start": v(25.5, -10.4) * mm, "mid": v(25.27, -9.83) * mm, "end": v(24.7, -9.6) * mm});
            skArc(sketch, "E17.12.0.9", {"start": v(23.3, -9.6) * mm, "mid": v(22.73, -9.83) * mm, "end": v(22.5, -10.4) * mm});
            skLineSegment(sketch, "E17.12.0.10", {"start": v(23.3, -9.6) * mm, "end": v(24.7, -9.6) * mm});
            skLineSegment(sketch, "E17.12.0.11", {"start": v(23.3, -37.6) * mm, "end": v(24.7, -37.6) * mm});
            skPoint(sketch, "E17.13.0.0", {"position": v(30.5, -37.6) * mm});
            skPoint(sketch, "E17.13.0.1", {"position": v(27.5, -37.6) * mm});
            skPoint(sketch, "E17.13.0.2", {"position": v(30.5, -9.6) * mm});
            skPoint(sketch, "E17.13.0.3", {"position": v(27.5, -9.6) * mm});
            skLineSegment(sketch, "E17.13.0.4", {"start": v(27.5, -10.4) * mm, "end": v(27.5, -36.8) * mm});
            skLineSegment(sketch, "E17.13.0.5", {"start": v(30.5, -10.4) * mm, "end": v(30.5, -36.8) * mm});
            skArc(sketch, "E17.13.0.6", {"start": v(29.7, -37.6) * mm, "mid": v(30.27, -37.37) * mm, "end": v(30.5, -36.8) * mm});
            skArc(sketch, "E17.13.0.7", {"start": v(27.5, -36.8) * mm, "mid": v(27.73, -37.37) * mm, "end": v(28.3, -37.6) * mm});
            skArc(sketch, "E17.13.0.8", {"start": v(30.5, -10.4) * mm, "mid": v(30.27, -9.83) * mm, "end": v(29.7, -9.6) * mm});
            skArc(sketch, "E17.13.0.9", {"start": v(28.3, -9.6) * mm, "mid": v(27.73, -9.83) * mm, "end": v(27.5, -10.4) * mm});
            skLineSegment(sketch, "E17.13.0.10", {"start": v(28.3, -9.6) * mm, "end": v(29.7, -9.6) * mm});
            skLineSegment(sketch, "E17.13.0.11", {"start": v(28.3, -37.6) * mm, "end": v(29.7, -37.6) * mm});
            skPoint(sketch, "E17.14.0.0", {"position": v(35.5, -37.6) * mm});
            skPoint(sketch, "E17.14.0.1", {"position": v(32.5, -37.6) * mm});
            skPoint(sketch, "E17.14.0.2", {"position": v(35.5, -9.6) * mm});
            skPoint(sketch, "E17.14.0.3", {"position": v(32.5, -9.6) * mm});
            skLineSegment(sketch, "E17.14.0.4", {"start": v(32.5, -10.4) * mm, "end": v(32.5, -36.8) * mm});
            skLineSegment(sketch, "E17.14.0.5", {"start": v(35.5, -10.4) * mm, "end": v(35.5, -36.8) * mm});
            skArc(sketch, "E17.14.0.6", {"start": v(34.7, -37.6) * mm, "mid": v(35.27, -37.37) * mm, "end": v(35.5, -36.8) * mm});
            skArc(sketch, "E17.14.0.7", {"start": v(32.5, -36.8) * mm, "mid": v(32.73, -37.37) * mm, "end": v(33.3, -37.6) * mm});
            skArc(sketch, "E17.14.0.8", {"start": v(35.5, -10.4) * mm, "mid": v(35.27, -9.83) * mm, "end": v(34.7, -9.6) * mm});
            skArc(sketch, "E17.14.0.9", {"start": v(33.3, -9.6) * mm, "mid": v(32.73, -9.83) * mm, "end": v(32.5, -10.4) * mm});
            skLineSegment(sketch, "E17.14.0.10", {"start": v(33.3, -9.6) * mm, "end": v(34.7, -9.6) * mm});
            skLineSegment(sketch, "E17.14.0.11", {"start": v(33.3, -37.6) * mm, "end": v(34.7, -37.6) * mm});
            skPoint(sketch, "E17.15.0.0", {"position": v(40.5, -37.6) * mm});
            skPoint(sketch, "E17.15.0.1", {"position": v(37.5, -37.6) * mm});
            skPoint(sketch, "E17.15.0.2", {"position": v(40.5, -9.6) * mm});
            skPoint(sketch, "E17.15.0.3", {"position": v(37.5, -9.6) * mm});
            skLineSegment(sketch, "E17.15.0.4", {"start": v(37.5, -10.4) * mm, "end": v(37.5, -36.8) * mm});
            skLineSegment(sketch, "E17.15.0.5", {"start": v(40.5, -10.4) * mm, "end": v(40.5, -36.8) * mm});
            skArc(sketch, "E17.15.0.6", {"start": v(39.7, -37.6) * mm, "mid": v(40.27, -37.37) * mm, "end": v(40.5, -36.8) * mm});
            skArc(sketch, "E17.15.0.7", {"start": v(37.5, -36.8) * mm, "mid": v(37.73, -37.37) * mm, "end": v(38.3, -37.6) * mm});
            skArc(sketch, "E17.15.0.8", {"start": v(40.5, -10.4) * mm, "mid": v(40.27, -9.83) * mm, "end": v(39.7, -9.6) * mm});
            skArc(sketch, "E17.15.0.9", {"start": v(38.3, -9.6) * mm, "mid": v(37.73, -9.83) * mm, "end": v(37.5, -10.4) * mm});
            skLineSegment(sketch, "E17.15.0.10", {"start": v(38.3, -9.6) * mm, "end": v(39.7, -9.6) * mm});
            skLineSegment(sketch, "E17.15.0.11", {"start": v(38.3, -37.6) * mm, "end": v(39.7, -37.6) * mm});
            skPoint(sketch, "E17.16.0.0", {"position": v(45.5, -37.6) * mm});
            skPoint(sketch, "E17.16.0.1", {"position": v(42.5, -37.6) * mm});
            skPoint(sketch, "E17.16.0.2", {"position": v(45.5, -9.6) * mm});
            skPoint(sketch, "E17.16.0.3", {"position": v(42.5, -9.6) * mm});
            skLineSegment(sketch, "E17.16.0.4", {"start": v(42.5, -10.4) * mm, "end": v(42.5, -36.8) * mm});
            skLineSegment(sketch, "E17.16.0.5", {"start": v(45.5, -10.4) * mm, "end": v(45.5, -36.8) * mm});
            skArc(sketch, "E17.16.0.6", {"start": v(44.7, -37.6) * mm, "mid": v(45.27, -37.37) * mm, "end": v(45.5, -36.8) * mm});
            skArc(sketch, "E17.16.0.7", {"start": v(42.5, -36.8) * mm, "mid": v(42.73, -37.37) * mm, "end": v(43.3, -37.6) * mm});
            skArc(sketch, "E17.16.0.8", {"start": v(45.5, -10.4) * mm, "mid": v(45.27, -9.83) * mm, "end": v(44.7, -9.6) * mm});
            skArc(sketch, "E17.16.0.9", {"start": v(43.3, -9.6) * mm, "mid": v(42.73, -9.83) * mm, "end": v(42.5, -10.4) * mm});
            skLineSegment(sketch, "E17.16.0.10", {"start": v(43.3, -9.6) * mm, "end": v(44.7, -9.6) * mm});
            skLineSegment(sketch, "E17.16.0.11", {"start": v(43.3, -37.6) * mm, "end": v(44.7, -37.6) * mm});
            skLineSegment(sketch, "E17.direction1", {"start": v(-34.5, -37.6) * mm, "end": v(-29.5, -37.6) * mm, "construction": true});
            skLineSegment(sketch, "E18.bottom", {"start": v(-37.5, 63.5) * mm, "end": v(-31.5, 63.5) * mm});
            skLineSegment(sketch, "E18.top", {"start": v(-37.5, 57.5) * mm, "end": v(-31.5, 57.5) * mm});
            skLineSegment(sketch, "E18.left", {"start": v(-37.5, 63.5) * mm, "end": v(-37.5, 57.5) * mm});
            skLineSegment(sketch, "E18.right", {"start": v(-31.5, 63.5) * mm, "end": v(-31.5, 57.5) * mm});
            skLineSegment(sketch, "E19.bottom", {"start": v(41.5, 63.5) * mm, "end": v(47.5, 63.5) * mm});
            skLineSegment(sketch, "E19.top", {"start": v(41.5, 57.5) * mm, "end": v(47.5, 57.5) * mm});
            skLineSegment(sketch, "E19.left", {"start": v(41.5, 63.5) * mm, "end": v(41.5, 57.5) * mm});
            skLineSegment(sketch, "E19.right", {"start": v(47.5, 63.5) * mm, "end": v(47.5, 57.5) * mm});
            skLineSegment(sketch, "E20.bottom", {"start": v(55, 50) * mm, "end": v(61, 50) * mm});
            skLineSegment(sketch, "E20.top", {"start": v(55, 44) * mm, "end": v(61, 44) * mm});
            skLineSegment(sketch, "E20.left", {"start": v(55, 50) * mm, "end": v(55, 44) * mm});
            skLineSegment(sketch, "E20.right", {"start": v(61, 50) * mm, "end": v(61, 44) * mm});
            skLineSegment(sketch, "E21.bottom", {"start": v(55, -34) * mm, "end": v(61, -34) * mm});
            skLineSegment(sketch, "E21.top", {"start": v(55, -40) * mm, "end": v(61, -40) * mm});
            skLineSegment(sketch, "E21.left", {"start": v(55, -34) * mm, "end": v(55, -40) * mm});
            skLineSegment(sketch, "E21.right", {"start": v(61, -34) * mm, "end": v(61, -40) * mm});
            skLineSegment(sketch, "E22.bottom", {"start": v(29.5, -47.5) * mm, "end": v(35.5, -47.5) * mm});
            skLineSegment(sketch, "E22.top", {"start": v(29.5, -53.5) * mm, "end": v(35.5, -53.5) * mm});
            skLineSegment(sketch, "E22.left", {"start": v(29.5, -47.5) * mm, "end": v(29.5, -53.5) * mm});
            skLineSegment(sketch, "E22.right", {"start": v(35.5, -47.5) * mm, "end": v(35.5, -53.5) * mm});
            skLineSegment(sketch, "E23.bottom", {"start": v(-35.5, -47.5) * mm, "end": v(-29.5, -47.5) * mm});
            skLineSegment(sketch, "E23.top", {"start": v(-35.5, -53.5) * mm, "end": v(-29.5, -53.5) * mm});
            skLineSegment(sketch, "E23.left", {"start": v(-35.5, -47.5) * mm, "end": v(-35.5, -53.5) * mm});
            skLineSegment(sketch, "E23.right", {"start": v(-29.5, -47.5) * mm, "end": v(-29.5, -53.5) * mm});
            skLineSegment(sketch, "E24.bottom", {"start": v(-51, 50) * mm, "end": v(-45, 50) * mm});
            skLineSegment(sketch, "E24.top", {"start": v(-51, 44) * mm, "end": v(-45, 44) * mm});
            skLineSegment(sketch, "E24.left", {"start": v(-51, 50) * mm, "end": v(-51, 44) * mm});
            skLineSegment(sketch, "E24.right", {"start": v(-45, 50) * mm, "end": v(-45, 44) * mm});
            skLineSegment(sketch, "E25.bottom", {"start": v(-51, -34) * mm, "end": v(-45, -34) * mm});
            skLineSegment(sketch, "E25.top", {"start": v(-51, -40) * mm, "end": v(-45, -40) * mm});
            skLineSegment(sketch, "E25.left", {"start": v(-51, -34) * mm, "end": v(-51, -40) * mm});
            skLineSegment(sketch, "E25.right", {"start": v(-45, -34) * mm, "end": v(-45, -40) * mm});
            const initialGuessF0  = {"E5": [-0.0465, -0.00249, 1, 0, 0.01497]};
            skSetInitialGuess(sketch, initialGuessF0);
            skSolve(sketch);
        }
        {
            var Q0;
            Q0=makeQuery(id+"F0.imprint","IMPRINT",FACE,{"disambiguationData":[TD([[makeQuery(id+"F0.imprint","IMPRINT",EDGE,{"derivedFrom":sQuery(id+"F0.wireOp",EDGE,"E0.bottom")}),-1.0]])]});
            extrude(context, id + "F1", {"entities" : qUnion([Q0]), "oppositeDirection" : true, "depth" : 1.5 * mm});
        }
        {
            var Q0;
            Q0=makeQuery(id+"F0.imprint","IMPRINT",FACE,{"disambiguationData":[TD([[makeQuery(id+"F0.imprint","IMPRINT",EDGE,{"derivedFrom":sQuery(id+"F0.wireOp",EDGE,"E1")}),1.0]])]});
            var Q1;
            Q1=makeQuery(id+"F0.imprint","IMPRINT",FACE,{"disambiguationData":[TD([[makeQuery(id+"F0.imprint","IMPRINT",EDGE,{"derivedFrom":sQuery(id+"F0.wireOp",EDGE,"E2")}),1.0]])]});
            var Q2;
            Q2=makeQuery(id+"F0.imprint","IMPRINT",FACE,{"disambiguationData":[TD([[makeQuery(id+"F0.imprint","IMPRINT",EDGE,{"derivedFrom":sQuery(id+"F0.wireOp",EDGE,"E4")}),1.0]])]});
            var Q3;
            Q3=makeQuery(id+"F0.imprint","IMPRINT",FACE,{"disambiguationData":[TD([[makeQuery(id+"F0.imprint","IMPRINT",EDGE,{"derivedFrom":sQuery(id+"F0.wireOp",EDGE,"E3")}),1.0]])]});
            extrude(context, id + "F2", {"entities" : qUnion([Q0, Q1, Q2, Q3]), "oppositeDirection" : true, "depth" : 22.5 * mm});
        }
        {
            var Q0;
            Q0=makeQuery(id+"F2.opExtrude","CAP_FACE",FACE,{"disambiguationData":[OSD([sQuery(id+"F0.wireOp",EDGE,"E2")])],"isStart":true});
            var sketch = newSketch(context, id + "F3", { "sketchPlane" : qUnion([Q0])});
            skCircle(sketch, "E26", {"center": v(55.5, 58) * mm, "radius": 3.25 * mm});
            skSolve(sketch);
        }
        {
            var Q0;
            Q0=makeQuery(id+"F3.imprint","IMPRINT",FACE,{"disambiguationData":[TD([[makeQuery(id+"F3.imprint","IMPRINT",EDGE,{"derivedFrom":sQuery(id+"F3.wireOp",EDGE,"E26")}),1.0]])]});
            extrude(context, id + "F4", {"entities" : qUnion([Q0]), "operationType" : NewBodyOperationType.REMOVE, "oppositeDirection" : true, "depth" : 20.5 * mm});
        }
        {
            var Q0;
            Q0=makeQuery(id+"F2.opExtrude","CAP_FACE",FACE,{"disambiguationData":[OSD([sQuery(id+"F0.wireOp",EDGE,"E1")])],"isStart":true});
            var sketch = newSketch(context, id + "F5", { "sketchPlane" : qUnion([Q0])});
            skCircle(sketch, "E27", {"center": v(-45.5, 58) * mm, "radius": 3.25 * mm});
            skSolve(sketch);
        }
        {
            var Q0;
            Q0=makeQuery(id+"F5.imprint","IMPRINT",FACE,{"disambiguationData":[TD([[makeQuery(id+"F5.imprint","IMPRINT",EDGE,{"derivedFrom":sQuery(id+"F5.wireOp",EDGE,"E27")}),1.0]])]});
            extrude(context, id + "F6", {"entities" : qUnion([Q0]), "operationType" : NewBodyOperationType.REMOVE, "oppositeDirection" : true, "depth" : 20.5 * mm});
        }
        {
            var Q0;
            Q0=makeQuery(id+"F2.opExtrude","CAP_FACE",FACE,{"disambiguationData":[OSD([sQuery(id+"F0.wireOp",EDGE,"E4")])],"isStart":true});
            var sketch = newSketch(context, id + "F7", { "sketchPlane" : qUnion([Q0])});
            skCircle(sketch, "E28", {"center": v(-45.5, -50) * mm, "radius": 3.1 * mm});
            skSolve(sketch);
        }
        {
            var Q0;
            Q0=makeQuery(id+"F7.imprint","IMPRINT",FACE,{"disambiguationData":[TD([[makeQuery(id+"F7.imprint","IMPRINT",EDGE,{"derivedFrom":sQuery(id+"F7.wireOp",EDGE,"E28")}),1.0]])]});
            extrude(context, id + "F8", {"entities" : qUnion([Q0]), "operationType" : NewBodyOperationType.REMOVE, "oppositeDirection" : true, "depth" : 20.5 * mm});
        }
        {
            var Q0;
            Q0=makeQuery(id+"F2.opExtrude","CAP_FACE",FACE,{"disambiguationData":[OSD([sQuery(id+"F0.wireOp",EDGE,"E3")])],"isStart":true});
            var sketch = newSketch(context, id + "F9", { "sketchPlane" : qUnion([Q0])});
            skCircle(sketch, "E29", {"center": v(55.5, -48) * mm, "radius": 3.25 * mm});
            skSolve(sketch);
        }
        {
            var Q0;
            Q0=makeQuery(id+"F9.imprint","IMPRINT",FACE,{"disambiguationData":[TD([[makeQuery(id+"F9.imprint","IMPRINT",EDGE,{"derivedFrom":sQuery(id+"F9.wireOp",EDGE,"E29")}),1.0]])]});
            extrude(context, id + "F10", {"entities" : qUnion([Q0]), "operationType" : NewBodyOperationType.REMOVE, "oppositeDirection" : true, "depth" : 20.5 * mm});
        }
        {
            var Q0;
            Q0=makeQuery(id+"F2.opExtrude","CAP_FACE",FACE,{"disambiguationData":[OSD([sQuery(id+"F0.wireOp",EDGE,"E4")])],"isStart":false});
            var sketch = newSketch(context, id + "F11", { "sketchPlane" : qUnion([Q0])});
            skCircle(sketch, "E30", {"center": v(-45.5, 50) * mm, "radius": 1.6 * mm});
            skSolve(sketch);
        }
        {
            var Q0;
            Q0=makeQuery(id+"F11.imprint","IMPRINT",FACE,{"disambiguationData":[TD([[makeQuery(id+"F11.imprint","IMPRINT",EDGE,{"derivedFrom":sQuery(id+"F11.wireOp",EDGE,"E30")}),1.0]])]});
            extrude(context, id + "F12", {"entities" : qUnion([Q0]), "operationType" : NewBodyOperationType.REMOVE, "oppositeDirection" : true, "depth" : 2.5 * mm});
        }
        {
            var Q0;
            Q0=makeQuery(id+"F2.opExtrude","CAP_FACE",FACE,{"disambiguationData":[OSD([sQuery(id+"F0.wireOp",EDGE,"E1")])],"isStart":false});
            var sketch = newSketch(context, id + "F13", { "sketchPlane" : qUnion([Q0])});
            skCircle(sketch, "E31", {"center": v(-45.5, -58) * mm, "radius": 1.6 * mm});
            skSolve(sketch);
        }
        {
            var Q0;
            Q0=makeQuery(id+"F13.imprint","IMPRINT",FACE,{"disambiguationData":[TD([[makeQuery(id+"F13.imprint","IMPRINT",EDGE,{"derivedFrom":sQuery(id+"F13.wireOp",EDGE,"E31")}),1.0]])]});
            extrude(context, id + "F14", {"entities" : qUnion([Q0]), "operationType" : NewBodyOperationType.REMOVE, "oppositeDirection" : true, "depth" : 2.5 * mm});
        }
        {
            var Q0;
            Q0=makeQuery(id+"F2.opExtrude","CAP_FACE",FACE,{"disambiguationData":[OSD([sQuery(id+"F0.wireOp",EDGE,"E2")])],"isStart":false});
            var sketch = newSketch(context, id + "F15", { "sketchPlane" : qUnion([Q0])});
            skCircle(sketch, "E32", {"center": v(55.5, -58) * mm, "radius": 1.6 * mm});
            skSolve(sketch);
        }
        {
            var Q0;
            Q0=makeQuery(id+"F15.imprint","IMPRINT",FACE,{"disambiguationData":[TD([[makeQuery(id+"F15.imprint","IMPRINT",EDGE,{"derivedFrom":sQuery(id+"F15.wireOp",EDGE,"E32")}),1.0]])]});
            extrude(context, id + "F16", {"entities" : qUnion([Q0]), "operationType" : NewBodyOperationType.REMOVE, "oppositeDirection" : true, "depth" : 2.5 * mm});
        }
        {
            var Q0;
            Q0=makeQuery(id+"F2.opExtrude","CAP_FACE",FACE,{"disambiguationData":[OSD([sQuery(id+"F0.wireOp",EDGE,"E3")])],"isStart":false});
            var sketch = newSketch(context, id + "F17", { "sketchPlane" : qUnion([Q0])});
            skCircle(sketch, "E33", {"center": v(55.5, 48) * mm, "radius": 1.6 * mm});
            skSolve(sketch);
        }
        {
            var Q0;
            Q0=makeQuery(id+"F17.imprint","IMPRINT",FACE,{"disambiguationData":[TD([[makeQuery(id+"F17.imprint","IMPRINT",EDGE,{"derivedFrom":sQuery(id+"F17.wireOp",EDGE,"E33")}),1.0]])]});
            extrude(context, id + "F18", {"entities" : qUnion([Q0]), "operationType" : NewBodyOperationType.REMOVE, "oppositeDirection" : true, "depth" : 2.5 * mm});
        }
        {
            var Q0;
            Q0=makeQuery(id+"F0.imprint","IMPRINT",FACE,{"disambiguationData":[TD([[makeQuery(id+"F0.imprint","IMPRINT",EDGE,{"derivedFrom":sQuery(id+"F0.wireOp",EDGE,"E5.sketch_text.stroke-0")}),-1.0]])]});
            extrude(context, id + "F19", {"entities" : qUnion([Q0]), "depth" : 1.5 * mm});
        }
        {
            var Q0;
            Q0=makeQuery(id+"F0.imprint","IMPRINT",FACE,{"disambiguationData":[TD([[makeQuery(id+"F0.imprint","IMPRINT",EDGE,{"derivedFrom":sQuery(id+"F0.wireOp",EDGE,"E5.sketch_text.stroke-28")}),-1.0]])]});
            var Q1;
            Q1=makeQuery(id+"F0.imprint","IMPRINT",FACE,{"disambiguationData":[TD([[makeQuery(id+"F0.imprint","IMPRINT",EDGE,{"derivedFrom":sQuery(id+"F0.wireOp",EDGE,"E5.sketch_text.stroke-32")}),-1.0]])]});
            var Q2;
            Q2=makeQuery(id+"F0.imprint","IMPRINT",FACE,{"disambiguationData":[TD([[makeQuery(id+"F0.imprint","IMPRINT",EDGE,{"derivedFrom":sQuery(id+"F0.wireOp",EDGE,"E5.sketch_text.stroke-46")}),-1.0]])]});
            var Q3;
            Q3=makeQuery(id+"F0.imprint","IMPRINT",FACE,{"disambiguationData":[TD([[makeQuery(id+"F0.imprint","IMPRINT",EDGE,{"derivedFrom":sQuery(id+"F0.wireOp",EDGE,"E5.sketch_text.stroke-71")}),-1.0]])]});
            var Q4;
            Q4=makeQuery(id+"F0.imprint","IMPRINT",FACE,{"disambiguationData":[TD([[makeQuery(id+"F0.imprint","IMPRINT",EDGE,{"derivedFrom":sQuery(id+"F0.wireOp",EDGE,"E5.sketch_text.stroke-97")}),-1.0]])]});
            var Q5;
            Q5=makeQuery(id+"F0.imprint","IMPRINT",FACE,{"disambiguationData":[TD([[makeQuery(id+"F0.imprint","IMPRINT",EDGE,{"derivedFrom":sQuery(id+"F0.wireOp",EDGE,"E5.sketch_text.stroke-113")}),-1.0]])]});
            var Q6;
            Q6=makeQuery(id+"F0.imprint","IMPRINT",FACE,{"disambiguationData":[TD([[makeQuery(id+"F0.imprint","IMPRINT",EDGE,{"derivedFrom":sQuery(id+"F0.wireOp",EDGE,"E5.sketch_text.stroke-119")}),-1.0]])]});
            extrude(context, id + "F20", {"entities" : qUnion([Q0, Q1, Q2, Q3, Q4, Q5, Q6]), "depth" : 1.5 * mm});
        }
        {
            var Q0;
            Q0=makeQuery(id+"F0.imprint","IMPRINT",FACE,{"disambiguationData":[TD([[makeQuery(id+"F0.imprint","IMPRINT",EDGE,{"derivedFrom":sQuery(id+"F0.wireOp",EDGE,"E18.bottom")}),-1.0]])]});
            var Q1;
            Q1=makeQuery(id+"F0.imprint","IMPRINT",FACE,{"disambiguationData":[TD([[makeQuery(id+"F0.imprint","IMPRINT",EDGE,{"derivedFrom":sQuery(id+"F0.wireOp",EDGE,"E19.bottom")}),-1.0]])]});
            var Q2;
            Q2=makeQuery(id+"F0.imprint","IMPRINT",FACE,{"disambiguationData":[TD([[makeQuery(id+"F0.imprint","IMPRINT",EDGE,{"derivedFrom":sQuery(id+"F0.wireOp",EDGE,"E20.bottom")}),-1.0]])]});
            var Q3;
            Q3=makeQuery(id+"F0.imprint","IMPRINT",FACE,{"disambiguationData":[TD([[makeQuery(id+"F0.imprint","IMPRINT",EDGE,{"derivedFrom":sQuery(id+"F0.wireOp",EDGE,"E21.bottom")}),-1.0]])]});
            var Q4;
            Q4=makeQuery(id+"F0.imprint","IMPRINT",FACE,{"disambiguationData":[TD([[makeQuery(id+"F0.imprint","IMPRINT",EDGE,{"derivedFrom":sQuery(id+"F0.wireOp",EDGE,"E22.bottom")}),-1.0]])]});
            var Q5;
            Q5=makeQuery(id+"F0.imprint","IMPRINT",FACE,{"disambiguationData":[TD([[makeQuery(id+"F0.imprint","IMPRINT",EDGE,{"derivedFrom":sQuery(id+"F0.wireOp",EDGE,"E23.bottom")}),-1.0]])]});
            extrude(context, id + "F21", {"entities" : qUnion([Q0, Q1, Q2, Q3, Q4, Q5]), "operationType" : NewBodyOperationType.ADD, "oppositeDirection" : true, "depth" : 11 * mm});
        }
        {
            var Q0;
            Q0=makeQuery(id+"F0.imprint","IMPRINT",FACE,{"disambiguationData":[TD([[makeQuery(id+"F0.imprint","IMPRINT",EDGE,{"derivedFrom":sQuery(id+"F0.wireOp",EDGE,"E24.bottom")}),-1.0]])]});
            var Q1;
            Q1=makeQuery(id+"F0.imprint","IMPRINT",FACE,{"disambiguationData":[TD([[makeQuery(id+"F0.imprint","IMPRINT",EDGE,{"derivedFrom":sQuery(id+"F0.wireOp",EDGE,"E25.bottom")}),-1.0]])]});
            extrude(context, id + "F22", {"entities" : qUnion([Q0, Q1]), "operationType" : NewBodyOperationType.ADD, "oppositeDirection" : true, "depth" : 11 * mm});
        }
        {
            var Q0;
            Q0=makeQuery(id+"F21.opExtrude","SWEPT_FACE",FACE,{"disambiguationData":[OSD([sQuery(id+"F0.wireOp",EDGE,"E20.right")])]});
            var sketch = newSketch(context, id + "F23", { "sketchPlane" : qUnion([Q0])});
            skCircle(sketch, "E34", {"center": v(47, -6.5) * mm, "radius": 1.5 * mm});
            skSolve(sketch);
        }
        {
            var Q0;
            Q0=makeQuery(id+"F23.imprint","IMPRINT",FACE,{"disambiguationData":[TD([[makeQuery(id+"F23.imprint","IMPRINT",EDGE,{"derivedFrom":sQuery(id+"F23.wireOp",EDGE,"E34")}),1.0]])]});
            extrude(context, id + "F24", {"entities" : qUnion([Q0]), "operationType" : NewBodyOperationType.REMOVE, "oppositeDirection" : true, "depth" : 5 * mm});
        }
        {
            var Q0;
            Q0=makeQuery(id+"F21.opExtrude","SWEPT_FACE",FACE,{"disambiguationData":[OSD([sQuery(id+"F0.wireOp",EDGE,"E21.right")])]});
            var sketch = newSketch(context, id + "F25", { "sketchPlane" : qUnion([Q0])});
            skCircle(sketch, "E35", {"center": v(-37, -6.5) * mm, "radius": 1.5 * mm});
            skPoint(sketch, "E35.centerSnap0", {"position": v(-37, -11) * mm});
            skSolve(sketch);
        }
        {
            var Q0;
            Q0=makeQuery(id+"F25.imprint","IMPRINT",FACE,{"disambiguationData":[TD([[makeQuery(id+"F25.imprint","IMPRINT",EDGE,{"derivedFrom":sQuery(id+"F25.wireOp",EDGE,"E35")}),1.0]])]});
            extrude(context, id + "F26", {"entities" : qUnion([Q0]), "operationType" : NewBodyOperationType.REMOVE, "oppositeDirection" : true, "depth" : 5 * mm});
        }
        {
            var Q0;
            Q0=makeQuery(id+"F21.opExtrude","SWEPT_FACE",FACE,{"disambiguationData":[OSD([sQuery(id+"F0.wireOp",EDGE,"E22.top")])]});
            var sketch = newSketch(context, id + "F27", { "sketchPlane" : qUnion([Q0])});
            skCircle(sketch, "E36", {"center": v(32.5, -6.5) * mm, "radius": 1.5 * mm});
            skPoint(sketch, "E36.centerSnap0", {"position": v(32.5, -11) * mm});
            skSolve(sketch);
        }
        {
            var Q0;
            Q0=makeQuery(id+"F27.imprint","IMPRINT",FACE,{"disambiguationData":[TD([[makeQuery(id+"F27.imprint","IMPRINT",EDGE,{"derivedFrom":sQuery(id+"F27.wireOp",EDGE,"E36")}),1.0]])]});
            extrude(context, id + "F28", {"entities" : qUnion([Q0]), "operationType" : NewBodyOperationType.REMOVE, "oppositeDirection" : true, "depth" : 5 * mm});
        }
        {
            var Q0;
            Q0=makeQuery(id+"F21.opExtrude","SWEPT_FACE",FACE,{"disambiguationData":[OSD([sQuery(id+"F0.wireOp",EDGE,"E23.top")])]});
            var sketch = newSketch(context, id + "F29", { "sketchPlane" : qUnion([Q0])});
            skCircle(sketch, "E37", {"center": v(-32.5, -6.5) * mm, "radius": 1.5 * mm});
            skPoint(sketch, "E37.centerSnap0", {"position": v(-32.5, -11) * mm});
            skSolve(sketch);
        }
        {
            var Q0;
            Q0=makeQuery(id+"F29.imprint","IMPRINT",FACE,{"disambiguationData":[TD([[makeQuery(id+"F29.imprint","IMPRINT",EDGE,{"derivedFrom":sQuery(id+"F29.wireOp",EDGE,"E37")}),1.0]])]});
            extrude(context, id + "F30", {"entities" : qUnion([Q0]), "operationType" : NewBodyOperationType.REMOVE, "oppositeDirection" : true, "depth" : 5 * mm});
        }
        {
            var Q0;
            Q0=makeQuery(id+"F22.opExtrude","SWEPT_FACE",FACE,{"disambiguationData":[OSD([sQuery(id+"F0.wireOp",EDGE,"E25.left")])]});
            var sketch = newSketch(context, id + "F31", { "sketchPlane" : qUnion([Q0])});
            skCircle(sketch, "E38", {"center": v(37, -6.5) * mm, "radius": 1.5 * mm});
            skPoint(sketch, "E38.centerSnap0", {"position": v(37, -11) * mm});
            skSolve(sketch);
        }
        {
            var Q0;
            Q0=makeQuery(id+"F31.imprint","IMPRINT",FACE,{"disambiguationData":[TD([[makeQuery(id+"F31.imprint","IMPRINT",EDGE,{"derivedFrom":sQuery(id+"F31.wireOp",EDGE,"E38")}),1.0]])]});
            extrude(context, id + "F32", {"entities" : qUnion([Q0]), "operationType" : NewBodyOperationType.REMOVE, "oppositeDirection" : true, "depth" : 5 * mm});
        }
        {
            var Q0;
            Q0=makeQuery(id+"F22.opExtrude","SWEPT_FACE",FACE,{"disambiguationData":[OSD([sQuery(id+"F0.wireOp",EDGE,"E24.left")])]});
            var sketch = newSketch(context, id + "F33", { "sketchPlane" : qUnion([Q0])});
            skCircle(sketch, "E39", {"center": v(-47, -6.5) * mm, "radius": 1.5 * mm});
            skPoint(sketch, "E39.centerSnap0", {"position": v(-47, -11) * mm});
            skSolve(sketch);
        }
        {
            var Q0;
            Q0=makeQuery(id+"F33.imprint","IMPRINT",FACE,{"disambiguationData":[TD([[makeQuery(id+"F33.imprint","IMPRINT",EDGE,{"derivedFrom":sQuery(id+"F33.wireOp",EDGE,"E39")}),1.0]])]});
            extrude(context, id + "F34", {"entities" : qUnion([Q0]), "operationType" : NewBodyOperationType.REMOVE, "oppositeDirection" : true, "depth" : 5 * mm});
        }
        {
            var Q0;
            Q0=makeQuery(id+"F21.opExtrude","SWEPT_FACE",FACE,{"disambiguationData":[OSD([sQuery(id+"F0.wireOp",EDGE,"E18.bottom")])]});
            var sketch = newSketch(context, id + "F35", { "sketchPlane" : qUnion([Q0])});
            skCircle(sketch, "E40", {"center": v(34.5, -6.5) * mm, "radius": 1.5 * mm});
            skPoint(sketch, "E40.centerSnap0", {"position": v(34.5, -11) * mm});
            skSolve(sketch);
        }
        {
            var Q0;
            Q0=makeQuery(id+"F35.imprint","IMPRINT",FACE,{"disambiguationData":[TD([[makeQuery(id+"F35.imprint","IMPRINT",EDGE,{"derivedFrom":sQuery(id+"F35.wireOp",EDGE,"E40")}),1.0]])]});
            extrude(context, id + "F36", {"entities" : qUnion([Q0]), "operationType" : NewBodyOperationType.REMOVE, "oppositeDirection" : true, "depth" : 5 * mm});
        }
        {
            var Q0;
            Q0=makeQuery(id+"F21.opExtrude","SWEPT_FACE",FACE,{"disambiguationData":[OSD([sQuery(id+"F0.wireOp",EDGE,"E19.bottom")])]});
            var sketch = newSketch(context, id + "F37", { "sketchPlane" : qUnion([Q0])});
            skCircle(sketch, "E41", {"center": v(-44.5, -6.5) * mm, "radius": 1.5 * mm});
            skPoint(sketch, "E41.centerSnap0", {"position": v(-44.5, -11) * mm});
            skSolve(sketch);
        }
        {
            var Q0;
            Q0=makeQuery(id+"F37.imprint","IMPRINT",FACE,{"disambiguationData":[TD([[makeQuery(id+"F37.imprint","IMPRINT",EDGE,{"derivedFrom":sQuery(id+"F37.wireOp",EDGE,"E41")}),1.0]])]});
            extrude(context, id + "F38", {"entities" : qUnion([Q0]), "operationType" : NewBodyOperationType.REMOVE, "oppositeDirection" : true, "depth" : 5 * mm});
        }
    });
